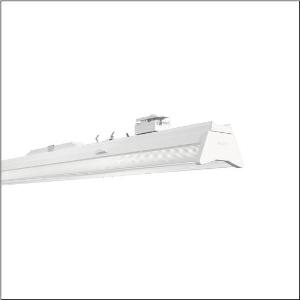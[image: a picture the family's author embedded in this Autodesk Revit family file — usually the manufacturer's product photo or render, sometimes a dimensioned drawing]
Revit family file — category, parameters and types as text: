
# Revit family: licross_r__21_performance_mo_52td16cn66xg_bcc0
name_source: partatom
category: Lighting Fixtures
units: mm (PartAtom-declared; Revit-internal decimal feet)

## family parameters
Cut with Voids When Loaded = No
Host = Face
Light Source = No
Part Type = Normal
Room Calculation Point = No
Round Connector Dimension = Use Diameter
Shared = No

## types (1)
- --- (1 x LED, 5970 lm, 32.8 W, 6500K)
    Apparent Load = 33 VA
    CIE Flux Codes = 66 88 96 79 100
    Color Rendering = 80
    Color Temperature = 6500K
    Default Elevation = 1800 mm
    Description = Licross® 21 Performance MO, luminaire insert, of sheet steel, galvanised, coil coated, white, length: 1.500mm, width: 120mm, height: 123mm, LED rated luminous flux: 5.970lm, light colour: 865, control gear: ON/OFF Multilumen, CLOi, with plug, 3-pole, with phase selection, mains connection: 220..240V, AC, 50/60Hz, start of lifetime: 33W, end of service life: 39W, halogen-free wiring, primary light control with lens, of plastic, primary optical cover: cover, of PMMA, light emission: direct/indirect distribution, primary light characteristic: symmetric, protection rating (complete): IP54, insulation class (complete): insulation class I (protective earthing), certification: CE, ENEC, UKCA, protection symbol: D if used in an environment with non-conductive dust loads with corresponding accessories, impact resistance: IK06, permissible ambient temperature for indoor applications: -35..+55°C, corresponds to IFS (International Featured Standards) requirements for safety and quality in the food industry, reducing of maximum allowable ambient temperature of 5°C with ceiling mounting, LABS conformity tested according to VDMA 24364:2018-05, packaging unit: 1 piece
    Height = 114 mm
    Lamp = 1 x LED
    Lamp Light Flux = 5970 lm
    Lamp Power = 32.8 W
    Lamp count = 1
    Length = 1500 mm
    Luminous efficacy = 182 lm/W
    Manufacturer = Siteco
    ModVariant = No
    Model = 52TD16CN66XG
    Mounting Place = Ceiling
    Mounting Type = Pendant
    Number of Poles = 1
    OnlyDefault = Yes
    Power Factor = 1
    Product Name = Licross® 21 Performance MO
    Product group = luminaire insert
    ProductGroupID = 901
    Protection Class = Protection class I
    Protection Degree = IP 54
    RLX_Detail_Level = 1
    RLX_Emergency_Light_Flux = 0 lm
    RLX_Emergency_Type = 0
    RLX_Emergency_Type_DB = No
    RlxData = <blob elided: 31733 chars, md5=8f5c11db>
    Socket = socket
    Standby Power = 0 W
    System Light Flux = 5970 lm
    System Power = 33 W
    Type Comments = factory setting: luminous flux: 100 % | (A | C | E) | 76 mA
    Type Image = l_1256138.jpg
    URL = http://relux.com
    VarID = @adj_006911
    Voltage = 0 V
    Weight = 0.00 kg
    Width = 120 mm

## geometry (parser evidence)
native form markers: Blend x4, Sweep x12
no freeform markers — native parametric forms only
